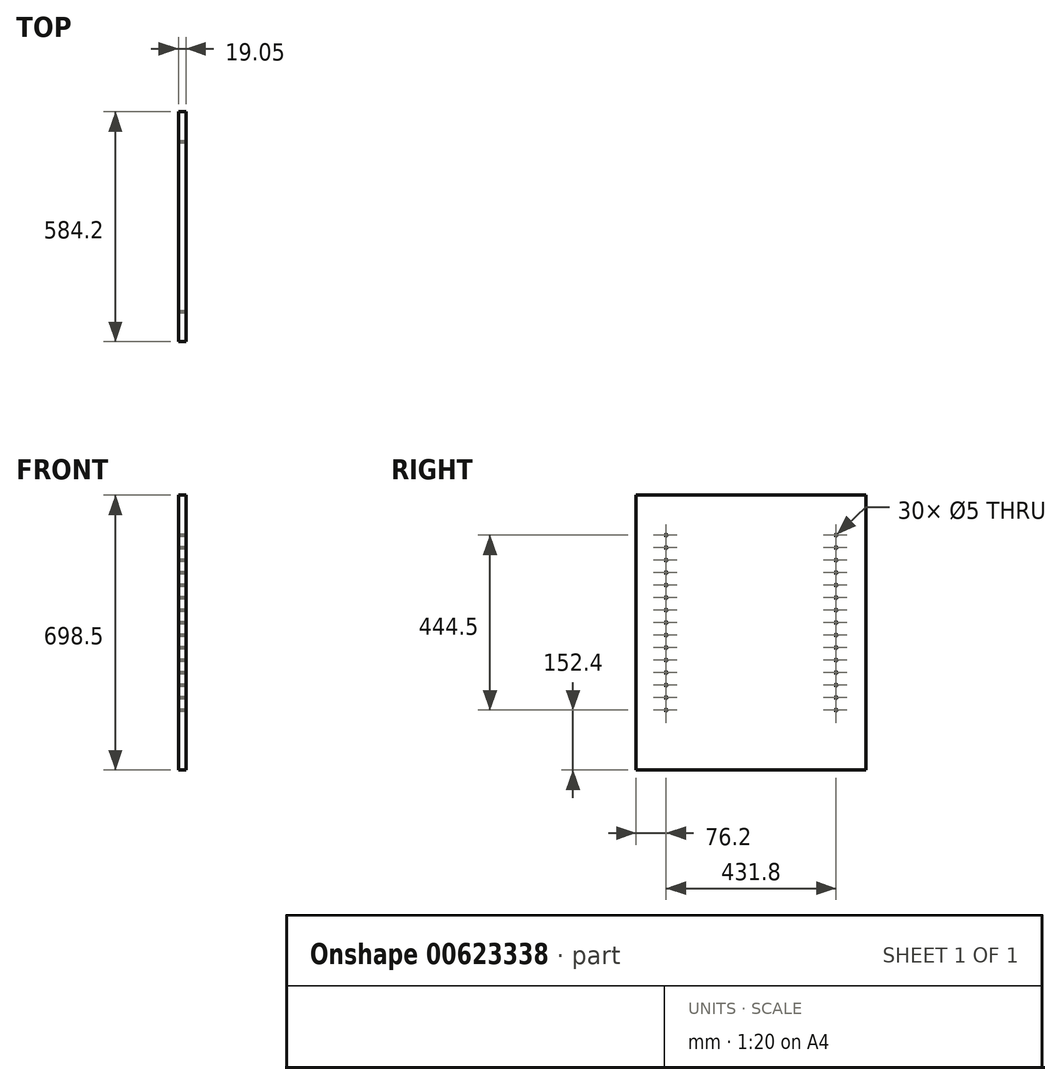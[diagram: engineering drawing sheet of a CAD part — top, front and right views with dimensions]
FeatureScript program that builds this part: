
annotation { "Feature Type Name" : "Feature", "Feature Type Description" : "" }
export const myFeature = defineFeature(function(context is Context, id is Id, definition is map)
    precondition{}
    {
        {
            var Q0;
            Q0=qCreatedBy(makeId("Right.planeOp"),FACE);
            var sketch = newSketch(context, id + "F0", { "sketchPlane" : qUnion([Q0])});
            skLineSegment(sketch, "E0.bottom", {"start": v(292.1, 349.25) * mm, "end": v(-292.1, 349.25) * mm});
            skLineSegment(sketch, "E0.top", {"start": v(292.1, -349.25) * mm, "end": v(-292.1, -349.25) * mm});
            skLineSegment(sketch, "E0.left", {"start": v(292.1, 349.25) * mm, "end": v(292.1, -349.25) * mm});
            skLineSegment(sketch, "E0.right", {"start": v(-292.1, 349.25) * mm, "end": v(-292.1, -349.25) * mm});
            skPoint(sketch, "E0.middle", {"position": v(0, 0) * mm});
            skSolve(sketch);
        }
        {
            var Q0;
            Q0=makeQuery(id+"F0.imprint","IMPRINT",FACE,{"disambiguationData":[TD([[makeQuery(id+"F0.imprint","IMPRINT",EDGE,{"derivedFrom":sQuery(id+"F0.wireOp",EDGE,"E0.bottom")}),1.0]])]});
            extrude(context, id + "F1", {"entities" : qUnion([Q0]), "depth" : 19.05 * mm, "offsetDistance" : 25.4 * mm});
        }
        {
            var Q0;
            Q0=makeQuery(id+"F1.opExtrude","CAP_FACE",FACE,{"disambiguationData":[OSD([sQuery(id+"F0.wireOp",EDGE,"E0.bottom"),sQuery(id+"F0.wireOp",EDGE,"E0.top"),sQuery(id+"F0.wireOp",EDGE,"E0.left"),sQuery(id+"F0.wireOp",EDGE,"E0.right")])],"isStart":false});
            var sketch = newSketch(context, id + "F2", { "sketchPlane" : qUnion([Q0])});
            skLineSegment(sketch, "E1", {"start": v(0, 349.25) * mm, "end": v(0, 215.9) * mm});
            skPoint(sketch, "E1.endSnap0", {"position": v(0, 349.25) * mm});
            skLineSegment(sketch, "E2.bottom", {"start": v(215.9, 184.15) * mm, "end": v(-215.9, 184.15) * mm});
            skLineSegment(sketch, "E2.top", {"start": v(215.9, 247.65) * mm, "end": v(-215.9, 247.65) * mm});
            skLineSegment(sketch, "E2.left", {"start": v(215.9, 184.15) * mm, "end": v(215.9, 247.65) * mm});
            skLineSegment(sketch, "E2.right", {"start": v(-215.9, 184.15) * mm, "end": v(-215.9, 247.65) * mm});
            skPoint(sketch, "E2.middle", {"position": v(0, 215.9) * mm});
            skLineSegment(sketch, "E3", {"start": v(0, 184.15) * mm, "end": v(0, 120.65) * mm});
            skLineSegment(sketch, "E4.bottom", {"start": v(215.9, 88.9) * mm, "end": v(-215.9, 88.9) * mm});
            skLineSegment(sketch, "E4.top", {"start": v(215.9, 152.4) * mm, "end": v(-215.9, 152.4) * mm});
            skLineSegment(sketch, "E4.left", {"start": v(215.9, 88.9) * mm, "end": v(215.9, 152.4) * mm});
            skLineSegment(sketch, "E4.right", {"start": v(-215.9, 88.9) * mm, "end": v(-215.9, 152.4) * mm});
            skPoint(sketch, "E4.middle", {"position": v(0, 120.65) * mm});
            skLineSegment(sketch, "E5", {"start": v(0, 88.9) * mm, "end": v(0, 25.4) * mm});
            skLineSegment(sketch, "E6.bottom", {"start": v(215.9, -6.35) * mm, "end": v(-215.9, -6.35) * mm});
            skLineSegment(sketch, "E6.top", {"start": v(215.9, 57.15) * mm, "end": v(-215.9, 57.15) * mm});
            skLineSegment(sketch, "E6.left", {"start": v(215.9, -6.35) * mm, "end": v(215.9, 57.15) * mm});
            skLineSegment(sketch, "E6.right", {"start": v(-215.9, -6.35) * mm, "end": v(-215.9, 57.15) * mm});
            skPoint(sketch, "E6.middle", {"position": v(0, 25.4) * mm});
            skLineSegment(sketch, "E7", {"start": v(0, -6.35) * mm, "end": v(0, -69.85) * mm});
            skLineSegment(sketch, "E8.bottom", {"start": v(-215.9, -38.1) * mm, "end": v(215.9, -38.1) * mm});
            skLineSegment(sketch, "E8.top", {"start": v(-215.9, -101.6) * mm, "end": v(215.9, -101.6) * mm});
            skLineSegment(sketch, "E8.left", {"start": v(-215.9, -38.1) * mm, "end": v(-215.9, -101.6) * mm});
            skLineSegment(sketch, "E8.right", {"start": v(215.9, -38.1) * mm, "end": v(215.9, -101.6) * mm});
            skPoint(sketch, "E8.middle", {"position": v(0, -69.85) * mm});
            skLineSegment(sketch, "E9", {"start": v(0, -101.6) * mm, "end": v(0, -165.1) * mm});
            skLineSegment(sketch, "E10.bottom", {"start": v(-215.9, -133.35) * mm, "end": v(215.9, -133.35) * mm});
            skLineSegment(sketch, "E10.top", {"start": v(-215.9, -196.85) * mm, "end": v(215.9, -196.85) * mm});
            skLineSegment(sketch, "E10.left", {"start": v(-215.9, -133.35) * mm, "end": v(-215.9, -196.85) * mm});
            skLineSegment(sketch, "E10.right", {"start": v(215.9, -133.35) * mm, "end": v(215.9, -196.85) * mm});
            skPoint(sketch, "E10.middle", {"position": v(0, -165.1) * mm});
            skPoint(sketch, "E11", {"position": v(-215.9, 247.65) * mm});
            skPoint(sketch, "E12", {"position": v(-215.9, 215.9) * mm});
            skPoint(sketch, "E13", {"position": v(-215.9, 184.15) * mm});
            skPoint(sketch, "E14", {"position": v(-215.9, 152.4) * mm});
            skPoint(sketch, "E15", {"position": v(-215.9, 120.65) * mm});
            skPoint(sketch, "E16", {"position": v(-215.9, 88.9) * mm});
            skPoint(sketch, "E17", {"position": v(-215.9, 57.15) * mm});
            skPoint(sketch, "E18", {"position": v(-215.9, 25.4) * mm});
            skPoint(sketch, "E19", {"position": v(-215.9, -6.35) * mm});
            skPoint(sketch, "E20", {"position": v(-215.9, -38.1) * mm});
            skPoint(sketch, "E21", {"position": v(-215.9, -69.85) * mm});
            skPoint(sketch, "E22", {"position": v(-215.9, -101.6) * mm});
            skPoint(sketch, "E23", {"position": v(-215.9, -133.35) * mm});
            skPoint(sketch, "E24", {"position": v(-215.9, -165.1) * mm});
            skPoint(sketch, "E25", {"position": v(-215.9, -196.85) * mm});
            skPoint(sketch, "E26", {"position": v(215.9, -196.85) * mm});
            skPoint(sketch, "E27", {"position": v(215.9, -165.1) * mm});
            skPoint(sketch, "E28", {"position": v(215.9, -133.35) * mm});
            skPoint(sketch, "E29", {"position": v(215.9, -101.6) * mm});
            skPoint(sketch, "E30", {"position": v(215.9, -69.85) * mm});
            skPoint(sketch, "E31", {"position": v(215.9, -38.1) * mm});
            skPoint(sketch, "E32", {"position": v(215.9, -6.35) * mm});
            skPoint(sketch, "E33", {"position": v(215.9, 25.4) * mm});
            skPoint(sketch, "E34", {"position": v(215.9, 57.15) * mm});
            skPoint(sketch, "E35", {"position": v(215.9, 88.9) * mm});
            skPoint(sketch, "E36", {"position": v(215.9, 120.65) * mm});
            skPoint(sketch, "E37", {"position": v(215.9, 152.4) * mm});
            skPoint(sketch, "E38", {"position": v(215.9, 184.15) * mm});
            skPoint(sketch, "E39", {"position": v(215.9, 215.9) * mm});
            skPoint(sketch, "E40", {"position": v(215.9, 247.65) * mm});
            skSolve(sketch);
        }
        {
            var Q0;
            Q0=sQuery(id+"F2.wireOp",VERTEX,"E11");
            var Q1;
            Q1=sQuery(id+"F2.wireOp",VERTEX,"E12");
            var Q2;
            Q2=sQuery(id+"F2.wireOp",VERTEX,"E13");
            var Q3;
            Q3=sQuery(id+"F2.wireOp",VERTEX,"E14");
            var Q4;
            Q4=sQuery(id+"F2.wireOp",VERTEX,"E15");
            var Q5;
            Q5=sQuery(id+"F2.wireOp",VERTEX,"E16");
            var Q6;
            Q6=sQuery(id+"F2.wireOp",VERTEX,"E17");
            var Q7;
            Q7=sQuery(id+"F2.wireOp",VERTEX,"E18");
            var Q8;
            Q8=sQuery(id+"F2.wireOp",VERTEX,"E19");
            var Q9;
            Q9=sQuery(id+"F2.wireOp",VERTEX,"E20");
            var Q10;
            Q10=sQuery(id+"F2.wireOp",VERTEX,"E21");
            var Q11;
            Q11=sQuery(id+"F2.wireOp",VERTEX,"E22");
            var Q12;
            Q12=sQuery(id+"F2.wireOp",VERTEX,"E23");
            var Q13;
            Q13=sQuery(id+"F2.wireOp",VERTEX,"E24");
            var Q14;
            Q14=sQuery(id+"F2.wireOp",VERTEX,"E25");
            var Q15;
            Q15=sQuery(id+"F2.wireOp",VERTEX,"E26");
            var Q16;
            Q16=sQuery(id+"F2.wireOp",VERTEX,"E27");
            var Q17;
            Q17=sQuery(id+"F2.wireOp",VERTEX,"E28");
            var Q18;
            Q18=sQuery(id+"F2.wireOp",VERTEX,"E29");
            var Q19;
            Q19=sQuery(id+"F2.wireOp",VERTEX,"E30");
            var Q20;
            Q20=sQuery(id+"F2.wireOp",VERTEX,"E31");
            var Q21;
            Q21=sQuery(id+"F2.wireOp",VERTEX,"E32");
            var Q22;
            Q22=sQuery(id+"F2.wireOp",VERTEX,"E33");
            var Q23;
            Q23=sQuery(id+"F2.wireOp",VERTEX,"E34");
            var Q24;
            Q24=sQuery(id+"F2.wireOp",VERTEX,"E35");
            var Q25;
            Q25=sQuery(id+"F2.wireOp",VERTEX,"E36");
            var Q26;
            Q26=sQuery(id+"F2.wireOp",VERTEX,"E37");
            var Q27;
            Q27=sQuery(id+"F2.wireOp",VERTEX,"E38");
            var Q28;
            Q28=sQuery(id+"F2.wireOp",VERTEX,"E39");
            var Q29;
            Q29=sQuery(id+"F2.wireOp",VERTEX,"E40");
            var Q30;
            Q30=makeQuery(id+"F1.opExtrude","SWEPT_BODY",BODY,{"disambiguationData":[OSD([sQuery(id+"F0.wireOp",EDGE,"E0.bottom"),sQuery(id+"F0.wireOp",EDGE,"E0.top"),sQuery(id+"F0.wireOp",EDGE,"E0.left"),sQuery(id+"F0.wireOp",EDGE,"E0.right")])]});
            hole(context, id + "F3", {"style" : HoleStyle.SIMPLE, "endStyle" : HoleEndStyle.BLIND, "holeDiameter" : 5 * mm, "majorDiameter" : 6.35 * mm, "holeDepth" : 14.22 * mm, "isTappedThrough" : true, "tappedDepth" : 12.7 * mm, "tapClearance" : 3, "startFromSketch" : true, "locations" : qUnion([Q0, Q1, Q2, Q3, Q4, Q5, Q6, Q7, Q8, Q9, Q10, Q11, Q12, Q13, Q14, Q15, Q16, Q17, Q18, Q19, Q20, Q21, Q22, Q23, Q24, Q25, Q26, Q27, Q28, Q29]), "scope" : qUnion([Q30])});
        }
    });
